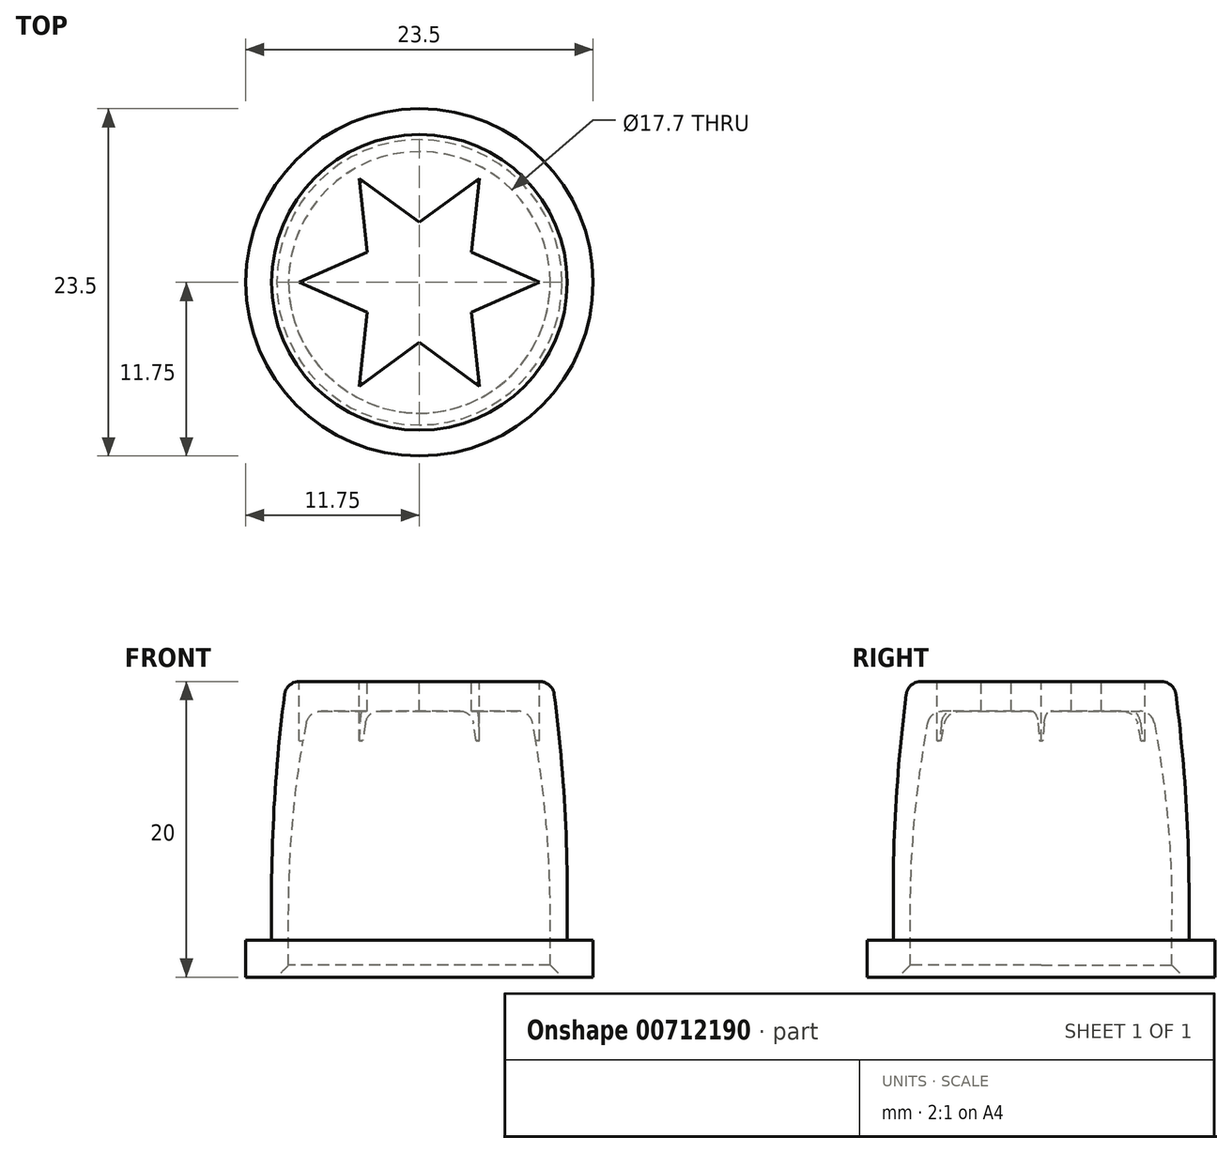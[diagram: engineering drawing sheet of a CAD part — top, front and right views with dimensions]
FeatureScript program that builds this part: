
annotation { "Feature Type Name" : "Feature", "Feature Type Description" : "" }
export const myFeature = defineFeature(function(context is Context, id is Id, definition is map)
    precondition{}
    {
        {
            var Q0;
            Q0=qCreatedBy(makeId("Front.planeOp"),FACE);
            var sketch = newSketch(context, id + "F0", { "sketchPlane" : qUnion([Q0])});
            skLineSegment(sketch, "E0", {"start": v(-11.75, 0) * mm, "end": v(-10.45, 0) * mm});
            skLineSegment(sketch, "E1", {"start": v(-10.45, 0) * mm, "end": v(-10.45, 1.2) * mm});
            skLineSegment(sketch, "E2", {"start": v(-10.45, 1.2) * mm, "end": v(-8.85, 1.2) * mm});
            skLineSegment(sketch, "E3", {"start": v(-8.85, 1.2) * mm, "end": v(-8.85, 4.2) * mm});
            skLineSegment(sketch, "E4", {"start": v(-11.75, 0) * mm, "end": v(-11.75, 2.5) * mm});
            skLineSegment(sketch, "E5", {"start": v(-11.75, 2.5) * mm, "end": v(-10, 2.5) * mm});
            skLineSegment(sketch, "E6", {"start": v(-10, 2.5) * mm, "end": v(-10, 5.5) * mm});
            skLineSegment(sketch, "E7", {"start": v(0, 20) * mm, "end": v(-8.13, 20) * mm});
            skLineSegment(sketch, "E8", {"start": v(0, 18) * mm, "end": v(-6.67, 18) * mm});
            skLineSegment(sketch, "E9", {"start": v(0, 20) * mm, "end": v(0, 18) * mm});
            skArc(sketch, "E10", {"start": v(-7.66, 17.18) * mm, "mid": v(-8.55, 10.72) * mm, "end": v(-8.85, 4.2) * mm});
            skArc(sketch, "E11", {"start": v(-9.12, 19.13) * mm, "mid": v(-9.78, 12.33) * mm, "end": v(-10, 5.5) * mm});
            skPoint(sketch, "E12.visualSharp", {"position": v(-7.5, 18) * mm});
            skPoint(sketch, "E13.visualSharp", {"position": v(-9, 20) * mm});
            skArc(sketch, "E14.filletArc", {"start": v(-8.13, 20) * mm, "mid": v(-8.79, 19.75) * mm, "end": v(-9.12, 19.13) * mm});
            skArc(sketch, "E15.filletArc", {"start": v(-6.67, 18) * mm, "mid": v(-7.31, 17.77) * mm, "end": v(-7.66, 17.18) * mm});
            skSolve(sketch);
        }
        {
            var Q0;
            Q0=makeQuery(id+"F0.imprint","IMPRINT",FACE,{"disambiguationData":[TD([[makeQuery(id+"F0.imprint","IMPRINT",EDGE,{"derivedFrom":sQuery(id+"F0.wireOp",EDGE,"E0")}),1.0]])]});
            var Q1;
            Q1=sQuery(id+"F0.wireOp",EDGE,"E9");
            revolve(context, id + "F1", {"surfaceOperationType" : NewSurfaceOperationType.NEW, "entities" : qUnion([Q0]), "axis" : qUnion([Q1]), "revolveType" : RevolveType.FULL});
        }
        {
            var Q0;
            Q0=makeQuery(id+"F1.opRevolve","SWEPT_FACE",FACE,{"disambiguationData":[OSD([sQuery(id+"F0.wireOp",EDGE,"E7")])]});
            var sketch = newSketch(context, id + "F2", { "sketchPlane" : qUnion([Q0])});
            skCircle(sketch, "E16.cCircle", {"center": v(0, 0) * mm, "radius": 8.13 * mm, "construction": true});
            skLineSegment(sketch, "E16.0", {"start": v(8.13, 0) * mm, "end": v(7.04, -4.06) * mm, "construction": true});
            skLineSegment(sketch, "E16.1", {"start": v(7.04, -4.06) * mm, "end": v(4.06, -7.04) * mm, "construction": true});
            skLineSegment(sketch, "E16.2", {"start": v(4.06, -7.04) * mm, "end": v(0, -8.13) * mm, "construction": true});
            skLineSegment(sketch, "E16.3", {"start": v(0, -8.13) * mm, "end": v(-4.06, -7.04) * mm, "construction": true});
            skLineSegment(sketch, "E16.4", {"start": v(-4.06, -7.04) * mm, "end": v(-7.04, -4.06) * mm, "construction": true});
            skLineSegment(sketch, "E16.5", {"start": v(-7.04, -4.06) * mm, "end": v(-8.13, 0) * mm, "construction": true});
            skLineSegment(sketch, "E16.6", {"start": v(-8.13, 0) * mm, "end": v(-7.04, 4.06) * mm, "construction": true});
            skLineSegment(sketch, "E16.7", {"start": v(-7.04, 4.06) * mm, "end": v(-4.06, 7.04) * mm, "construction": true});
            skLineSegment(sketch, "E16.8", {"start": v(-4.06, 7.04) * mm, "end": v(0, 8.13) * mm, "construction": true});
            skLineSegment(sketch, "E16.9", {"start": v(0, 8.13) * mm, "end": v(4.06, 7.04) * mm, "construction": true});
            skLineSegment(sketch, "E16.10", {"start": v(4.06, 7.04) * mm, "end": v(7.04, 4.06) * mm, "construction": true});
            skLineSegment(sketch, "E16.11", {"start": v(7.04, 4.06) * mm, "end": v(8.13, 0) * mm, "construction": true});
            skLineSegment(sketch, "E17", {"start": v(0, 8.13) * mm, "end": v(0, 0) * mm, "construction": true});
            skLineSegment(sketch, "E18", {"start": v(7.04, 4.06) * mm, "end": v(0, 0) * mm, "construction": true});
            skLineSegment(sketch, "E19", {"start": v(7.04, -4.06) * mm, "end": v(0, 0) * mm, "construction": true});
            skLineSegment(sketch, "E20", {"start": v(0, -8.13) * mm, "end": v(0, 0) * mm, "construction": true});
            skLineSegment(sketch, "E21", {"start": v(-7.04, -4.06) * mm, "end": v(0, 0) * mm, "construction": true});
            skLineSegment(sketch, "E22", {"start": v(-7.04, 4.06) * mm, "end": v(0, 0) * mm, "construction": true});
            skLineSegment(sketch, "E23", {"start": v(0, 4.06) * mm, "end": v(4.06, 7.04) * mm});
            skLineSegment(sketch, "E24", {"start": v(4.06, 7.04) * mm, "end": v(3.52, 2.03) * mm});
            skLineSegment(sketch, "E25", {"start": v(3.52, 2.03) * mm, "end": v(8.13, 0) * mm});
            skLineSegment(sketch, "E26", {"start": v(8.13, 0) * mm, "end": v(3.52, -2.03) * mm});
            skLineSegment(sketch, "E27", {"start": v(3.52, -2.03) * mm, "end": v(4.06, -7.04) * mm});
            skLineSegment(sketch, "E28", {"start": v(4.06, -7.04) * mm, "end": v(0, -4.06) * mm});
            skLineSegment(sketch, "E29", {"start": v(0, -4.06) * mm, "end": v(-4.06, -7.04) * mm});
            skLineSegment(sketch, "E30", {"start": v(-4.06, -7.04) * mm, "end": v(-3.52, -2.03) * mm});
            skLineSegment(sketch, "E31", {"start": v(-3.52, -2.03) * mm, "end": v(-8.13, 0) * mm});
            skLineSegment(sketch, "E32", {"start": v(-8.13, 0) * mm, "end": v(-3.52, 2.03) * mm});
            skLineSegment(sketch, "E33", {"start": v(-3.52, 2.03) * mm, "end": v(-4.06, 7.04) * mm});
            skLineSegment(sketch, "E34", {"start": v(-4.06, 7.04) * mm, "end": v(0, 4.06) * mm});
            skSolve(sketch);
        }
        {
            var Q0;
            Q0=makeQuery(id+"F2.imprint","IMPRINT",FACE,{"disambiguationData":[TD([[makeQuery(id+"F2.imprint","IMPRINT",EDGE,{"derivedFrom":sQuery(id+"F2.wireOp",EDGE,"E23")}),-1.0]])]});
            extrude(context, id + "F3", {"entities" : qUnion([Q0]), "operationType" : NewBodyOperationType.REMOVE, "oppositeDirection" : true, "depth" : 4 * mm, "offsetDistance" : 25 * mm});
        }
        {
            var Q0;
            Q0=makeQuery(id+"F1.opRevolve","SWEPT_EDGE",EDGE,{"disambiguationData":[OSD([sQuery(id+"F0.wireOp",EDGE,"E1"),sQuery(id+"F0.wireOp",EDGE,"E2")])]});
            chamfer(context, id + "F4", {"entities" : qUnion([Q0]), "width" : 2 * mm, "tangentPropagation" : true});
        }
    });
